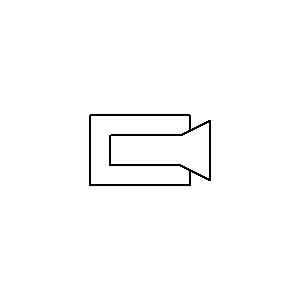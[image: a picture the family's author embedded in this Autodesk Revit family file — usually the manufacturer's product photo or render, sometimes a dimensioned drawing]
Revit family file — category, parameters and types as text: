
# Revit family: Gira_126566
name_source: partatom
category: Electrical Fixtures
revit_build: Autodesk Revit 2017 (Build: 20160225_1515(x64)
units: mm (PartAtom-declared; Revit-internal decimal feet)

## family parameters
Cut with Voids When Loaded = No
Host = Face
Maintain Annotation Orientation = Yes
Part Type = Normal
Room Calculation Point = No
Round Connector Dimension = Use Diameter
Shared = No

## types (1)
- Colour camera door st. Gira TX_44 (WP FM) p.white
    Available = No
    BIM (1) = https://media.stage.bim.site
    Category = External camera door communication
    Colour = White
    Data sheet (1) = https://katalog.gira.de
    Default Elevation = 1219 mm
    Description = Colour camera door st. TX_44 PW,Colour camera for door station,,pure white,Features:,- Installation in a conventional flush-mounted device box.,- Fits in the cover frames of the Gira TX_44 switch range.,- Modular design, allowing easy installation and expandability.,- Signal transmission and supply of the audio and video components via reverse-polarity-protected and short-circuit-proof 2-wire bus.,- Extension of door stations by a colour camera with automatic day or night switching.,- LEDs ensure steady illumination of the field of view at close proximity in night mode.,- Camera can be manually swivelled 20 horizontally and vertically. In combination with the wide-angle lens, a very wide field of view of the door entry area results.,- Automatic background lighting compensation.,- Automatic white balance.,- Automatic gain control (AGC).,- Integrated temperature-dependent camera heating.,- Sprayed-water proof cover plate.,- Camera cover plate made of shock-resistant plastic. Easy to replace if damaged, e.g. due to vandalism.,,Notes :,- The colour camera may not be positioned directly beneath a light.,- Suitable for use in a Gira energy profile.,- Not suitable for use in a Gira energy profile with light.
    GTIN = 4010337265665
    HAN = 126566
    HeinzeBIM = https://bimportal.heinze.de
    Installation technique = Bus system
    Manufacturer = Gira
    Manufacturer URL = https://www.gira.de
    Material = Other
    Mounting method = Built-in
    Name = Colour camera door st. Gira TX_44 (WP FM) p.white
    URL = http://katalog.gira.de

## geometry (parser evidence)
native form markers: Sweep x2
no freeform markers — native parametric forms only
